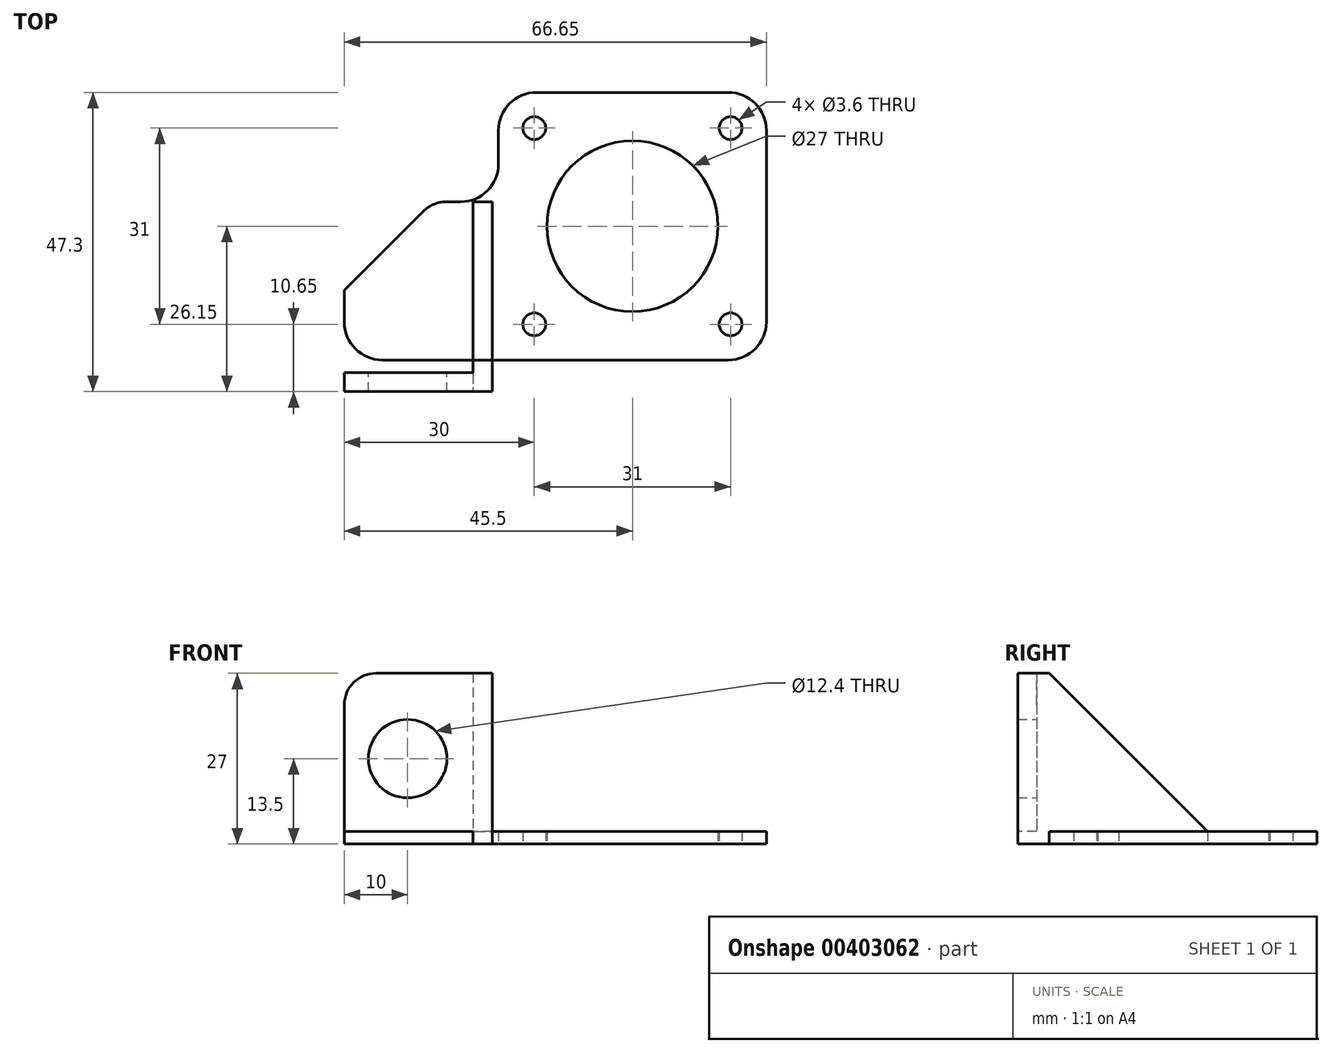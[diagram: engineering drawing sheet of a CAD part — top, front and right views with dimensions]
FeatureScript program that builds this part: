
annotation { "Feature Type Name" : "Feature", "Feature Type Description" : "" }
export const myFeature = defineFeature(function(context is Context, id is Id, definition is map)
    precondition{}
    {
        {
            var Q0;
            Q0=qCreatedBy(makeId("Top.planeOp"),FACE);
            var sketch = newSketch(context, id + "F0", { "sketchPlane" : qUnion([Q0])});
            skLineSegment(sketch, "E0.bottom", {"start": v(21.15, 21.15) * mm, "end": v(-21.15, 21.15) * mm});
            skLineSegment(sketch, "E0.top", {"start": v(21.15, -21.15) * mm, "end": v(-21.15, -21.15) * mm});
            skLineSegment(sketch, "E0.left", {"start": v(21.15, 21.15) * mm, "end": v(21.15, -21.15) * mm});
            skLineSegment(sketch, "E0.right", {"start": v(-21.15, 21.15) * mm, "end": v(-21.15, -21.15) * mm});
            skPoint(sketch, "E0.middle", {"position": v(0, 0) * mm});
            skLineSegment(sketch, "E1.bottom", {"start": v(15.5, 15.5) * mm, "end": v(-15.5, 15.5) * mm, "construction": true});
            skLineSegment(sketch, "E1.top", {"start": v(15.5, -15.5) * mm, "end": v(-15.5, -15.5) * mm, "construction": true});
            skLineSegment(sketch, "E1.left", {"start": v(15.5, 15.5) * mm, "end": v(15.5, -15.5) * mm, "construction": true});
            skLineSegment(sketch, "E1.right", {"start": v(-15.5, 15.5) * mm, "end": v(-15.5, -15.5) * mm, "construction": true});
            skCircle(sketch, "E2", {"center": v(-15.5, 15.5) * mm, "radius": 1.8 * mm});
            skCircle(sketch, "E3", {"center": v(15.5, 15.5) * mm, "radius": 1.8 * mm});
            skCircle(sketch, "E4", {"center": v(15.5, -15.5) * mm, "radius": 1.8 * mm});
            skCircle(sketch, "E5", {"center": v(-15.5, -15.5) * mm, "radius": 1.8 * mm});
            skCircle(sketch, "E6", {"center": v(0, 0) * mm, "radius": 13.5 * mm});
            skLineSegment(sketch, "E7.bottom", {"start": v(-21.15, -21.15) * mm, "end": v(-45.5, -21.15) * mm});
            skLineSegment(sketch, "E7.top", {"start": v(-21.15, 3.85) * mm, "end": v(-45.5, 3.85) * mm});
            skLineSegment(sketch, "E7.left", {"start": v(-21.15, -21.15) * mm, "end": v(-21.15, 3.85) * mm});
            skLineSegment(sketch, "E7.right", {"start": v(-45.5, -21.15) * mm, "end": v(-45.5, 3.85) * mm});
            skLineSegment(sketch, "E8.bottom", {"start": v(-45.5, -21.15) * mm, "end": v(-21.16, -21.15) * mm});
            skLineSegment(sketch, "E8.top", {"start": v(-45.5, -26.15) * mm, "end": v(-21.16, -26.15) * mm});
            skLineSegment(sketch, "E8.left", {"start": v(-45.5, -21.15) * mm, "end": v(-45.5, -26.15) * mm});
            skLineSegment(sketch, "E8.right", {"start": v(-21.16, -21.15) * mm, "end": v(-21.16, -26.15) * mm});
            skSolve(sketch);
        }
        {
            var Q0;
            Q0=makeQuery(id+"F0.imprint","IMPRINT",FACE,{"disambiguationData":[TD([[makeQuery(id+"F0.imprint","IMPRINT",EDGE,{"derivedFrom":sQuery(id+"F0.wireOp",EDGE,"E0.bottom")}),1.0]])]});
            var Q1;
            Q1=makeQuery(id+"F0.imprint","IMPRINT",FACE,{"disambiguationData":[TD([[makeQuery(id+"F0.imprint","IMPRINT",EDGE,{"derivedFrom":sQuery(id+"F0.wireOp",EDGE,"E7.bottom")}),-1.0]])]});
            var Q2;
            Q2=makeQuery(id+"F0.imprint","IMPRINT",FACE,{"disambiguationData":[TD([[makeQuery(id+"F0.imprint","IMPRINT",EDGE,{"derivedFrom":sQuery(id+"F0.wireOp",EDGE,"E8.bottom")}),-1.0]])]});
            extrude(context, id + "F1", {"entities" : qUnion([Q0, Q1, Q2]), "depth" : 2 * mm});
        }
        {
            var Q0;
            Q0=qCreatedBy(makeId("Top.planeOp"),FACE);
            var sketch = newSketch(context, id + "F2", { "sketchPlane" : qUnion([Q0])});
            skLineSegment(sketch, "E9.bottom", {"start": v(-22.16, 3.85) * mm, "end": v(-25.16, 3.85) * mm});
            skLineSegment(sketch, "E9.top", {"start": v(-22.16, -26.15) * mm, "end": v(-25.16, -26.15) * mm});
            skLineSegment(sketch, "E9.left", {"start": v(-22.16, 3.85) * mm, "end": v(-22.16, -26.15) * mm});
            skLineSegment(sketch, "E9.right", {"start": v(-25.16, 3.85) * mm, "end": v(-25.16, -26.15) * mm});
            skSolve(sketch);
        }
        {
            var Q0;
            Q0=qSketchRegion(id+"F2",true);
            extrude(context, id + "F3", {"entities" : qUnion([Q0]), "operationType" : NewBodyOperationType.ADD, "depth" : 27 * mm});
        }
        {
            var Q0;
            {var subQ0=sQuery(id+"F0.wireOp",EDGE,"E8.left");var subQ1=sQuery(id+"F0.wireOp",EDGE,"E7.right");var subQ2=sQuery(id+"F0.wireOp",EDGE,"E8.top");var subQ3=sQuery(id+"F0.wireOp",EDGE,"E7.top");Q0=makeQuery(id+"F3.boolean.opBoolean","SPLIT",FACE,{"disambiguationData":[TD([makeQuery(id+"F3.opExtrude","SWEPT_FACE",FACE,{"disambiguationData":[OSD([sQuery(id+"F2.wireOp",EDGE,"E9.right")])]})])],"derivedFrom":makeQuery(id+"F1.opExtrude","CAP_FACE",FACE,{"disambiguationData":[OSD([sQuery(id+"F0.wireOp",EDGE,"E0.bottom"),sQuery(id+"F0.wireOp",EDGE,"E0.top"),sQuery(id+"F0.wireOp",EDGE,"E0.left"),sQuery(id+"F0.wireOp",EDGE,"E0.right"),sQuery(id+"F0.wireOp",EDGE,"E2"),sQuery(id+"F0.wireOp",EDGE,"E3"),sQuery(id+"F0.wireOp",EDGE,"E4"),sQuery(id+"F0.wireOp",EDGE,"E5"),sQuery(id+"F0.wireOp",EDGE,"E6"),sQuery(id+"F0.wireOp",EDGE,"E7.bottom"),subQ3,subQ1,subQ2,subQ0,sQuery(id+"F0.wireOp",EDGE,"E8.right")])],"isStart":false})});}
            var sketch = newSketch(context, id + "F4", { "sketchPlane" : qUnion([Q0])});
            skLineSegment(sketch, "E10.bottom", {"start": v(-45.5, -23.15) * mm, "end": v(-25.16, -23.15) * mm});
            skLineSegment(sketch, "E10.top", {"start": v(-45.5, -26.15) * mm, "end": v(-25.16, -26.15) * mm});
            skLineSegment(sketch, "E10.left", {"start": v(-45.5, -23.15) * mm, "end": v(-45.5, -26.15) * mm});
            skLineSegment(sketch, "E10.right", {"start": v(-25.16, -23.15) * mm, "end": v(-25.16, -26.15) * mm});
            skSolve(sketch);
        }
        {
            var Q0;
            Q0=makeQuery(id+"F4.imprint","IMPRINT",FACE,{"disambiguationData":[TD([[makeQuery(id+"F4.imprint","IMPRINT",EDGE,{"derivedFrom":sQuery(id+"F4.wireOp",EDGE,"E10.bottom")}),-1.0]])]});
            extrude(context, id + "F5", {"entities" : qUnion([Q0]), "operationType" : NewBodyOperationType.ADD, "depth" : 25 * mm});
        }
        {
            var Q0;
            Q0=makeQuery(id+"F5.opExtrude","SWEPT_FACE",FACE,{"disambiguationData":[OSD([sQuery(id+"F4.wireOp",EDGE,"E10.bottom")])]});
            var sketch = newSketch(context, id + "F6", { "sketchPlane" : qUnion([Q0])});
            skCircle(sketch, "E11", {"center": v(35.5, 13.5) * mm, "radius": 6.2 * mm});
            skCircle(sketch, "E12", {"center": v(35.5, 13.5) * mm, "radius": 8.65 * mm, "construction": true});
            skSolve(sketch);
        }
        {
            var Q0;
            Q0=makeQuery(id+"F3.opExtrude","CAP_EDGE",EDGE,{"disambiguationData":[OSD([sQuery(id+"F2.wireOp",EDGE,"E9.bottom")])],"isStart":false});
            chamfer(context, id + "F7", {"entities" : qUnion([Q0]), "width" : 25 * mm, "tangentPropagation" : true});
        }
        {
            var Q0;
            Q0=makeQuery(id+"F1.opExtrude","SWEPT_EDGE",EDGE,{"disambiguationData":[OSD([sQuery(id+"F0.wireOp",EDGE,"E7.top"),sQuery(id+"F0.wireOp",EDGE,"E7.right")])]});
            chamfer(context, id + "F8", {"entities" : qUnion([Q0]), "width" : 14 * mm, "tangentPropagation" : true});
        }
        {
            var Q0;
            {var subQ0=sQuery(id+"F0.wireOp",EDGE,"E7.right");Q0=makeQuery(id+"F8.opChamfer","BLEND_EDGE",EDGE,{"blendedFrom":[makeQuery(id+"F1.opExtrude","SWEPT_EDGE",EDGE,{"disambiguationData":[OSD([sQuery(id+"F0.wireOp",EDGE,"E7.top"),subQ0])]}),makeQuery(id+"F5.boolean.opBoolean","MERGE",FACE,{"derivedFrom":[makeQuery(id+"F1.opExtrude","SWEPT_FACE",FACE,{"disambiguationData":[OSD([subQ0,sQuery(id+"F0.wireOp",EDGE,"E8.left")])]}),makeQuery(id+"F5.opExtrude","SWEPT_FACE",FACE,{"disambiguationData":[OSD([sQuery(id+"F4.wireOp",EDGE,"E10.left")])]})]})],"blendedInto":[makeQuery(id+"F5.boolean.opBoolean","MERGE",FACE,{"derivedFrom":[makeQuery(id+"F1.opExtrude","SWEPT_FACE",FACE,{"disambiguationData":[OSD([subQ0,sQuery(id+"F0.wireOp",EDGE,"E8.left")])]}),makeQuery(id+"F5.opExtrude","SWEPT_FACE",FACE,{"disambiguationData":[OSD([sQuery(id+"F4.wireOp",EDGE,"E10.left")])]})]})]});}
            var Q1;
            {var subQ0=sQuery(id+"F0.wireOp",EDGE,"E7.top");Q1=makeQuery(id+"F8.opChamfer","BLEND_EDGE",EDGE,{"blendedFrom":[makeQuery(id+"F1.opExtrude","SWEPT_EDGE",EDGE,{"disambiguationData":[OSD([subQ0,sQuery(id+"F0.wireOp",EDGE,"E7.right")])]}),makeQuery(id+"F3.boolean.opBoolean","MERGE",FACE,{"derivedFrom":[makeQuery(id+"F1.opExtrude","SWEPT_FACE",FACE,{"disambiguationData":[OSD([subQ0])]}),makeQuery(id+"F3.opExtrude","SWEPT_FACE",FACE,{"disambiguationData":[OSD([sQuery(id+"F2.wireOp",EDGE,"E9.bottom")])]})]})],"blendedInto":[makeQuery(id+"F3.boolean.opBoolean","MERGE",FACE,{"derivedFrom":[makeQuery(id+"F1.opExtrude","SWEPT_FACE",FACE,{"disambiguationData":[OSD([subQ0])]}),makeQuery(id+"F3.opExtrude","SWEPT_FACE",FACE,{"disambiguationData":[OSD([sQuery(id+"F2.wireOp",EDGE,"E9.bottom")])]})]})]});}
            var Q2;
            Q2=makeQuery(id+"F1.opExtrude","SWEPT_EDGE",EDGE,{"disambiguationData":[OSD([sQuery(id+"F0.wireOp",EDGE,"E8.top"),sQuery(id+"F0.wireOp",EDGE,"E8.right")])]});
            var Q3;
            Q3=makeQuery(id+"F5.opExtrude","CAP_EDGE",EDGE,{"disambiguationData":[OSD([sQuery(id+"F4.wireOp",EDGE,"E10.left")])],"isStart":false});
            fillet(context, id + "F9", {"entities" : qUnion([Q0, Q1, Q2, Q3]), "radius" : 5 * mm, "tangentPropagation" : true, "allowEdgeOverflow" : false});
        }
        {
            var Q0;
            Q0=makeQuery(id+"F1.opExtrude","SWEPT_EDGE",EDGE,{"disambiguationData":[OSD([sQuery(id+"F0.wireOp",EDGE,"E0.top"),sQuery(id+"F0.wireOp",EDGE,"E0.left")])]});
            var Q1;
            Q1=makeQuery(id+"F1.opExtrude","SWEPT_EDGE",EDGE,{"disambiguationData":[OSD([sQuery(id+"F0.wireOp",EDGE,"E0.bottom"),sQuery(id+"F0.wireOp",EDGE,"E0.left")])]});
            var Q2;
            Q2=makeQuery(id+"F1.opExtrude","SWEPT_EDGE",EDGE,{"disambiguationData":[OSD([sQuery(id+"F0.wireOp",EDGE,"E0.bottom"),sQuery(id+"F0.wireOp",EDGE,"E0.right")])]});
            var Q3;
            Q3=makeQuery(id+"F1.opExtrude","SWEPT_EDGE",EDGE,{"disambiguationData":[OSD([sQuery(id+"F0.wireOp",EDGE,"E0.right"),sQuery(id+"F0.wireOp",EDGE,"E7.top"),sQuery(id+"F0.wireOp",EDGE,"E7.left")])]});
            var Q4;
            Q4=makeQuery(id+"F1.opExtrude","SWEPT_EDGE",EDGE,{"disambiguationData":[OSD([sQuery(id+"F0.wireOp",EDGE,"E7.bottom"),sQuery(id+"F0.wireOp",EDGE,"E8.bottom"),sQuery(id+"F0.wireOp",EDGE,"E8.right")])]});
            fillet(context, id + "F10", {"entities" : qUnion([Q0, Q1, Q2, Q3, Q4]), "radius" : 6 * mm, "tangentPropagation" : true, "allowEdgeOverflow" : false});
        }
        {
            var Q0;
            Q0=qSketchRegion(id+"F6",true);
            var Q1;
            Q1=makeQuery(id+"F5.boolean.opBoolean","MERGE",FACE,{"derivedFrom":[makeQuery(id+"F3.boolean.opBoolean","MERGE",FACE,{"derivedFrom":[makeQuery(id+"F1.opExtrude","SWEPT_FACE",FACE,{"disambiguationData":[OSD([sQuery(id+"F0.wireOp",EDGE,"E8.top")])]}),makeQuery(id+"F3.opExtrude","SWEPT_FACE",FACE,{"disambiguationData":[OSD([sQuery(id+"F2.wireOp",EDGE,"E9.top")])]})]}),makeQuery(id+"F5.opExtrude","SWEPT_FACE",FACE,{"disambiguationData":[OSD([sQuery(id+"F4.wireOp",EDGE,"E10.top")])]})]});
            extrude(context, id + "F11", {"entities" : qUnion([Q0, Q1]), "operationType" : NewBodyOperationType.REMOVE, "oppositeDirection" : true, "depth" : 25 * mm});
        }
    });
